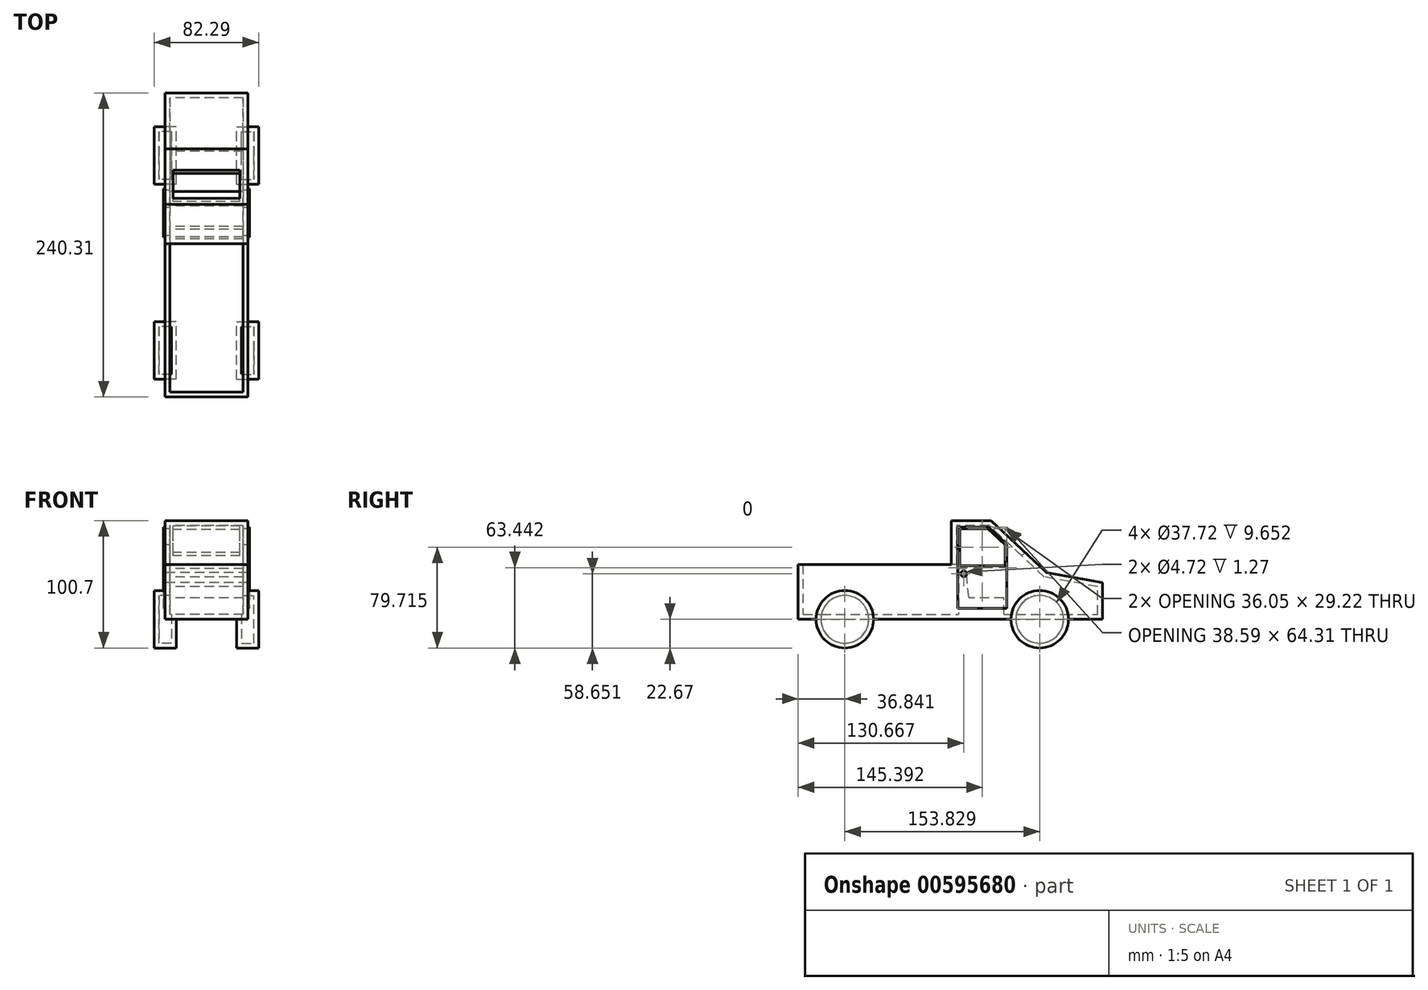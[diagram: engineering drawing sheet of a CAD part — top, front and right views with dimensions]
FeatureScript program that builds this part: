
annotation { "Feature Type Name" : "Feature", "Feature Type Description" : "" }
export const myFeature = defineFeature(function(context is Context, id is Id, definition is map)
    precondition{}
    {
        {
            var Q0;
            Q0=qCreatedBy(makeId("Right.planeOp"),FACE);
            var sketch = newSketch(context, id + "F0", { "sketchPlane" : qUnion([Q0])});
            skLineSegment(sketch, "E0", {"start": v(0, 0) * mm, "end": v(122.06, 0) * mm});
            skLineSegment(sketch, "E1", {"start": v(122.06, 0) * mm, "end": v(122.06, 29.01) * mm});
            skLineSegment(sketch, "E2", {"start": v(122.06, 29.01) * mm, "end": v(77.79, 37.01) * mm});
            skLineSegment(sketch, "E3", {"start": v(77.79, 37.01) * mm, "end": v(34.04, 78.03) * mm});
            skLineSegment(sketch, "E4", {"start": v(34.04, 78.03) * mm, "end": v(2.77, 77.77) * mm});
            skLineSegment(sketch, "E5", {"start": v(2.77, 77.77) * mm, "end": v(2.77, 43.22) * mm});
            skLineSegment(sketch, "E6", {"start": v(2.77, 43.22) * mm, "end": v(-118.25, 43.22) * mm});
            skLineSegment(sketch, "E7", {"start": v(-118.25, 43.22) * mm, "end": v(-118.25, 0) * mm});
            skLineSegment(sketch, "E8", {"start": v(-118.25, 0) * mm, "end": v(-77.8, 0) * mm});
            skLineSegment(sketch, "E9", {"start": v(-77.8, 0) * mm, "end": v(0, 0) * mm});
            skSolve(sketch);
        }
        {
            var Q0;
            Q0 = qSketchRegion(id + "F0", true);
            extrude(context, id + "F1", {"entities" : qUnion([Q0]), "depth" : 65.53 * mm, "offsetDistance" : 25.4 * mm});
        }
        {
            var Q0;
            Q0=makeQuery(id+"F1.opExtrude","CAP_FACE",FACE,{"disambiguationData":[OSD([sQuery(id+"F0.wireOp",EDGE,"E0"),sQuery(id+"F0.wireOp",EDGE,"E1"),sQuery(id+"F0.wireOp",EDGE,"E2"),sQuery(id+"F0.wireOp",EDGE,"E3"),sQuery(id+"F0.wireOp",EDGE,"E4"),sQuery(id+"F0.wireOp",EDGE,"E5"),sQuery(id+"F0.wireOp",EDGE,"E6"),sQuery(id+"F0.wireOp",EDGE,"E7"),sQuery(id+"F0.wireOp",EDGE,"E8"),sQuery(id+"F0.wireOp",EDGE,"E9")])],"isStart":false});
            var sketch = newSketch(context, id + "F2", { "sketchPlane" : qUnion([Q0])});
            skCircle(sketch, "E10", {"center": v(-81.4, 0) * mm, "radius": 22.67 * mm});
            skCircle(sketch, "E11", {"center": v(72.42, 0) * mm, "radius": 22.67 * mm});
            skSolve(sketch);
        }
        {
            var Q0;
            Q0 = qSketchRegion(id + "F2", true);
            extrude(context, id + "F3", {"entities" : qUnion([Q0]), "operationType" : NewBodyOperationType.ADD, "oppositeDirection" : true, "depth" : 8.9 * mm, "offsetDistance" : 25.4 * mm, "hasSecondDirection" : true, "secondDirectionOppositeDirection" : false, "secondDirectionDepth" : 8.38 * mm});
        }
        {
            var Q0;
            Q0=makeQuery(id+"F1.opExtrude","SWEPT_EDGE",EDGE,{"disambiguationData":[OSD([sQuery(id+"F0.wireOp",EDGE,"E6"),sQuery(id+"F0.wireOp",EDGE,"E7")])]});
            cPoint(context, id + "F4", {"entities" : qUnion([Q0]), "parameter" : 0.5});
        }
        {
            var Q0;
            Q0=qCreatedBy(makeId("Right.planeOp"),FACE);
            var Q1;
            Q1 = qCreatedBy(id + "F4" ,VERTEX);
            cPlane(context, id + "F5", {"entities" : qUnion([Q0, Q1]), "cplaneType" : CPlaneType.PLANE_POINT, "offset" : 25.4 * mm, "width" : 152.4 * mm, "height" : 152.4 * mm});
        }
        {
            var Q0;
            Q0=makeQuery(id+"F1.opExtrude","SWEPT_BODY",BODY,{"disambiguationData":[OSD([sQuery(id+"F0.wireOp",EDGE,"E0"),sQuery(id+"F0.wireOp",EDGE,"E1"),sQuery(id+"F0.wireOp",EDGE,"E2"),sQuery(id+"F0.wireOp",EDGE,"E3"),sQuery(id+"F0.wireOp",EDGE,"E4"),sQuery(id+"F0.wireOp",EDGE,"E5"),sQuery(id+"F0.wireOp",EDGE,"E6"),sQuery(id+"F0.wireOp",EDGE,"E7"),sQuery(id+"F0.wireOp",EDGE,"E8"),sQuery(id+"F0.wireOp",EDGE,"E9")])]});
            var Q1;
            Q1=qCreatedBy(id+"F5.planeOp",FACE);
            mirror(context, id + "F6", {"operationType" : NewBodyOperationType.ADD, "entities" : qUnion([Q0]), "mirrorPlane" : qUnion([Q1])});
        }
        {
            var Q0;
            Q0=makeQuery(id+"F1.opExtrude","SWEPT_FACE",FACE,{"disambiguationData":[OSD([sQuery(id+"F0.wireOp",EDGE,"E6")])]});
            shell(context, id + "F7", {"entities" : qUnion([Q0]), "thickness" : 3.8 * mm});
        }
        {
            var Q0;
            Q0=makeQuery(id+"F1.opExtrude","CAP_FACE",FACE,{"disambiguationData":[OSD([sQuery(id+"F0.wireOp",EDGE,"E0"),sQuery(id+"F0.wireOp",EDGE,"E1"),sQuery(id+"F0.wireOp",EDGE,"E2"),sQuery(id+"F0.wireOp",EDGE,"E3"),sQuery(id+"F0.wireOp",EDGE,"E4"),sQuery(id+"F0.wireOp",EDGE,"E5"),sQuery(id+"F0.wireOp",EDGE,"E6"),sQuery(id+"F0.wireOp",EDGE,"E7"),sQuery(id+"F0.wireOp",EDGE,"E8"),sQuery(id+"F0.wireOp",EDGE,"E9")])],"isStart":false});
            var sketch = newSketch(context, id + "F8", { "sketchPlane" : qUnion([Q0])});
            skLineSegment(sketch, "E12.0", {"start": v(77.79, 37.01) * mm, "end": v(34.04, 78.03) * mm, "construction": true});
            skLineSegment(sketch, "E13.0", {"start": v(34.04, 78.03) * mm, "end": v(2.77, 77.77) * mm, "construction": true});
            skLineSegment(sketch, "E14.0", {"start": v(2.77, 77.77) * mm, "end": v(2.77, 43.22) * mm, "construction": true});
            skLineSegment(sketch, "E15.0", {"start": v(-58.74, 0) * mm, "end": v(49.75, 0) * mm, "construction": true});
            skLineSegment(sketch, "E16.0", {"start": v(7.85, 72.73) * mm, "end": v(7.85, 43.22) * mm});
            skLineSegment(sketch, "E16.1", {"start": v(32.05, 72.93) * mm, "end": v(7.85, 72.73) * mm});
            skLineSegment(sketch, "E16.2", {"start": v(46.43, 59.44) * mm, "end": v(32.05, 72.93) * mm});
            skLineSegment(sketch, "E17", {"start": v(7.85, 43.22) * mm, "end": v(7.85, 8.62) * mm});
            skLineSegment(sketch, "E18", {"start": v(7.85, 8.62) * mm, "end": v(46.43, 8.62) * mm});
            skLineSegment(sketch, "E19", {"start": v(46.43, 8.62) * mm, "end": v(46.43, 59.44) * mm});
            skCircle(sketch, "E20", {"center": v(12.42, 35.98) * mm, "radius": 2.36 * mm});
            skSolve(sketch);
        }
        {
            var Q0;
            Q0 = qSketchRegion(id + "F8", true);
            extrude(context, id + "F9", {"entities" : qUnion([Q0]), "depth" : 1.27 * mm, "offsetDistance" : 25.4 * mm});
        }
        {
            var Q0;
            Q0=makeQuery(id+"F9.opExtrude","SWEPT_BODY",BODY,{"disambiguationData":[OSD([sQuery(id+"F8.wireOp",EDGE,"E16.0"),sQuery(id+"F8.wireOp",EDGE,"E16.1"),sQuery(id+"F8.wireOp",EDGE,"E16.2"),sQuery(id+"F8.wireOp",EDGE,"E17"),sQuery(id+"F8.wireOp",EDGE,"E18"),sQuery(id+"F8.wireOp",EDGE,"E19"),sQuery(id+"F8.wireOp",EDGE,"E20")])]});
            var Q1;
            Q1=qCreatedBy(id+"F5.planeOp",FACE);
            mirror(context, id + "F10", {"operationType" : NewBodyOperationType.ADD, "entities" : qUnion([Q0]), "mirrorPlane" : qUnion([Q1])});
        }
        {
            var Q0;
            Q0=makeQuery(id+"F10.opPattern","COPY",FACE,{"derivedFrom":makeQuery(id+"F9.opExtrude","CAP_FACE",FACE,{"disambiguationData":[OSD([sQuery(id+"F8.wireOp",EDGE,"E16.0"),sQuery(id+"F8.wireOp",EDGE,"E16.1"),sQuery(id+"F8.wireOp",EDGE,"E16.2"),sQuery(id+"F8.wireOp",EDGE,"E17"),sQuery(id+"F8.wireOp",EDGE,"E18"),sQuery(id+"F8.wireOp",EDGE,"E19"),sQuery(id+"F8.wireOp",EDGE,"E20")])],"isStart":false}),"instanceName":"1"});
            var sketch = newSketch(context, id + "F11", { "sketchPlane" : qUnion([Q0])});
            skLineSegment(sketch, "E21.0", {"start": v(-9.12, 71.48) * mm, "end": v(-9.12, 42.44) * mm});
            skLineSegment(sketch, "E21.1", {"start": v(-31.55, 71.65) * mm, "end": v(-9.12, 71.48) * mm});
            skLineSegment(sketch, "E21.2", {"start": v(-45.16, 58.9) * mm, "end": v(-31.55, 71.65) * mm});
            skLineSegment(sketch, "E21.3", {"start": v(-45.16, 42.44) * mm, "end": v(-45.16, 58.9) * mm});
            skLineSegment(sketch, "E22", {"start": v(-45.16, 42.44) * mm, "end": v(-9.12, 42.44) * mm});
            skSolve(sketch);
        }
        {
            var Q0;
            Q0 = qSketchRegion(id + "F11", true);
            extrude(context, id + "F12", {"entities" : qUnion([Q0]), "operationType" : NewBodyOperationType.REMOVE, "endBound" : BoundingType.THROUGH_ALL, "oppositeDirection" : true, "depth" : 25.4 * mm, "offsetDistance" : 25.4 * mm});
        }
        {
            var Q0;
            Q0=makeQuery(id+"F1.opExtrude","SWEPT_FACE",FACE,{"disambiguationData":[OSD([sQuery(id+"F0.wireOp",EDGE,"E3")])]});
            var sketch = newSketch(context, id + "F13", { "sketchPlane" : qUnion([Q0])});
            skLineSegment(sketch, "E23.0", {"start": v(59.18, -22.18) * mm, "end": v(6.35, -22.18) * mm});
            skLineSegment(sketch, "E23.1", {"start": v(59.18, 8.24) * mm, "end": v(59.18, -22.18) * mm});
            skLineSegment(sketch, "E23.3", {"start": v(6.35, 8.24) * mm, "end": v(6.35, -22.18) * mm});
            skLineSegment(sketch, "E24", {"start": v(59.18, 8.24) * mm, "end": v(6.35, 8.24) * mm});
            skSolve(sketch);
        }
        {
            var Q0;
            Q0 = qSketchRegion(id + "F13", true);
            extrude(context, id + "F14", {"entities" : qUnion([Q0]), "operationType" : NewBodyOperationType.REMOVE, "endBound" : BoundingType.UP_TO_NEXT, "oppositeDirection" : true, "depth" : 25.4 * mm, "offsetDistance" : 25.4 * mm});
        }
        {
            var Q0;
            {var subQ0=sQuery(id+"F0.wireOp",EDGE,"E9");var subQ1=sQuery(id+"F0.wireOp",EDGE,"E8");var subQ2=sQuery(id+"F0.wireOp",EDGE,"E7");var subQ3=sQuery(id+"F0.wireOp",EDGE,"E6");var subQ4=sQuery(id+"F0.wireOp",EDGE,"E5");var subQ5=sQuery(id+"F0.wireOp",EDGE,"E4");var subQ6=sQuery(id+"F0.wireOp",EDGE,"E3");var subQ7=sQuery(id+"F0.wireOp",EDGE,"E2");var subQ8=sQuery(id+"F0.wireOp",EDGE,"E1");var subQ9=sQuery(id+"F0.wireOp",EDGE,"E0");Q0=makeQuery(id+"F7.opShell","OFFSET_FACE",FACE,{"disambiguationData":[OSD([subQ9,subQ8,subQ7,subQ6,subQ5,subQ4,subQ3,subQ2,subQ1,subQ0]),TDD([makeQuery(id+"F1.opExtrude","CAP_FACE",FACE,{"disambiguationData":[OSD([subQ9,subQ8,subQ7,subQ6,subQ5,subQ4,subQ3,subQ2,subQ1,subQ0])],"isStart":true})])]});}
            var sketch = newSketch(context, id + "F15", { "sketchPlane" : qUnion([Q0])});
            skLineSegment(sketch, "E25", {"start": v(8.39, 40) * mm, "end": v(8.39, 3.81) * mm});
            skLineSegment(sketch, "E26", {"start": v(8.39, 3.81) * mm, "end": v(44.1, 3.8) * mm});
            skLineSegment(sketch, "E27", {"start": v(44.1, 3.8) * mm, "end": v(44.1, 16.98) * mm});
            skLineSegment(sketch, "E28", {"start": v(44.1, 16.98) * mm, "end": v(16.5, 16.98) * mm});
            skLineSegment(sketch, "E29", {"start": v(16.5, 16.98) * mm, "end": v(14.26, 40) * mm});
            skLineSegment(sketch, "E30", {"start": v(14.26, 40) * mm, "end": v(8.39, 40) * mm});
            skSolve(sketch);
        }
        {
            var Q0;
            Q0 = qSketchRegion(id + "F15", true);
            extrude(context, id + "F16", {"entities" : qUnion([Q0]), "operationType" : NewBodyOperationType.ADD, "endBound" : BoundingType.UP_TO_NEXT, "depth" : 25.4 * mm, "offsetDistance" : 25.4 * mm});
        }
    });
